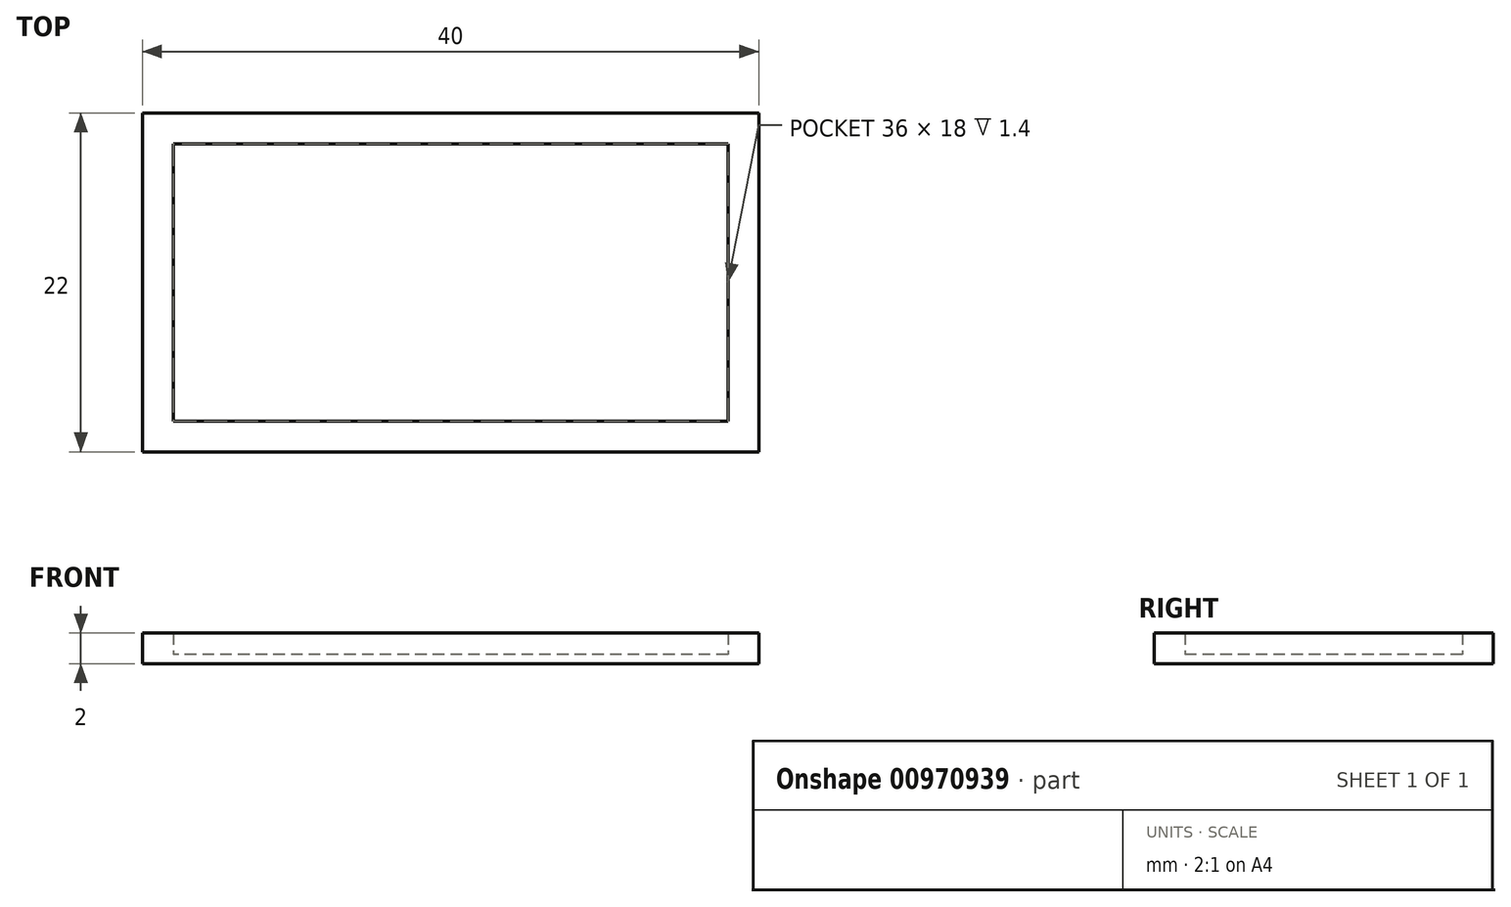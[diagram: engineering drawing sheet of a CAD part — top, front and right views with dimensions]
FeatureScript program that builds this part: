
annotation { "Feature Type Name" : "Feature", "Feature Type Description" : "" }
export const myFeature = defineFeature(function(context is Context, id is Id, definition is map)
    precondition{}
    {
        {
            var Q0;
            Q0=qCreatedBy(makeId("Top.planeOp"),FACE);
            var sketch = newSketch(context, id + "F0", { "sketchPlane" : qUnion([Q0])});
            skLineSegment(sketch, "E0.bottom", {"start": v(18, 9) * mm, "end": v(-18, 9) * mm});
            skLineSegment(sketch, "E0.top", {"start": v(18, -9) * mm, "end": v(-18, -9) * mm});
            skLineSegment(sketch, "E0.left", {"start": v(18, 9) * mm, "end": v(18, -9) * mm});
            skLineSegment(sketch, "E0.right", {"start": v(-18, 9) * mm, "end": v(-18, -9) * mm});
            skPoint(sketch, "E0.middle", {"position": v(0, 0) * mm});
            skLineSegment(sketch, "E1.bottom", {"start": v(20, 11) * mm, "end": v(-20, 11) * mm});
            skLineSegment(sketch, "E1.top", {"start": v(20, -11) * mm, "end": v(-20, -11) * mm});
            skLineSegment(sketch, "E1.left", {"start": v(20, 11) * mm, "end": v(20, -11) * mm});
            skLineSegment(sketch, "E1.right", {"start": v(-20, 11) * mm, "end": v(-20, -11) * mm});
            skSolve(sketch);
        }
        {
            var Q0;
            Q0=makeQuery(id+"F0.imprint","IMPRINT",FACE,{"disambiguationData":[TD([[makeQuery(id+"F0.imprint","IMPRINT",EDGE,{"derivedFrom":sQuery(id+"F0.wireOp",EDGE,"E0.bottom")}),-1.0]])]});
            extrude(context, id + "F1", {"entities" : qUnion([Q0]), "depth" : 2 * mm, "offsetDistance" : 25 * mm});
        }
        {
            var Q0;
            Q0=makeQuery(id+"F0.imprint","IMPRINT",FACE,{"disambiguationData":[TD([[makeQuery(id+"F0.imprint","IMPRINT",EDGE,{"derivedFrom":sQuery(id+"F0.wireOp",EDGE,"E0.bottom")}),1.0]])]});
            extrude(context, id + "F2", {"entities" : qUnion([Q0]), "operationType" : NewBodyOperationType.ADD, "depth" : .6 * mm, "offsetDistance" : 25 * mm});
        }
    });
